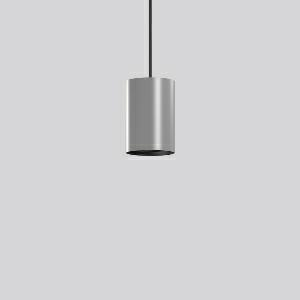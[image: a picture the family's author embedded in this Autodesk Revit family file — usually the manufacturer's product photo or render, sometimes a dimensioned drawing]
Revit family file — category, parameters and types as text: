
# Revit family: deecos_p_maxi_911538_004_3_76_b0c1
name_source: partatom
category: Lighting Fixtures
units: mm (PartAtom-declared; Revit-internal decimal feet)

## family parameters
Cut with Voids When Loaded = No
Host = Face
Light Source = No
Part Type = Normal
Room Calculation Point = No
Round Connector Dimension = Use Diameter
Shared = No

## types (1)
- DEECOS P maxi (1 x LED Modul 935, 4400 lm, 3500)
    Apparent Load = 35 VA
    Approval mark = CE
    CIE Flux Codes = 100 100 100 100 100
    Color Rendering = 92
    Color Temperature = 3500
    Default Elevation = 1800 mm
    Description = Series: DEECOS P maxi
Cylindrical pendant luminaire. Housing: die-cast aluminium, powder-coated. Canopy made of powder-coated sheet steel with magnetic attachment. Optical assembly with reflector made of MIRO-Silver with 98% total light reflection for outstanding efficiency - can be changed without tools. Best colour rendering index Ra>90. Transparent suspension cable 2 m, can be shortened. High quality converter without flickering and stroboscopic effect. The following accessories can be mounted without use of tools: interchangeable lenses, honeycomb louvre, clear and frosted diffusers, white interchangeable plastic ring. Decorative recessed suspension set available as accessory. 
Colour: silver
Diameter: 123 mm
Height: 181 mm
Suspension length: 2000 mm
Lamp: LED
Socket: without socket
Colour temperature: 3500K
Colour rendering index (CRI): 92
System power: 35 W
Rated luminous flux: 4400 lm
Luminous efficiency: 126 lm/W
Control gear: Converter, dimmable, DALI
Protection class: I
Type of protection: IP 20
    Height = 181 mm
    Lamp = 1 x LED Modul 935
    Lamp Light Flux = 4400 lm
    Lamp count = 1
    Length = 123 mm
    Lifetime = 50000 h
    Luminous efficacy = 126 lm/W
    Manufacturer = RZB
    ModVariant = No
    Model = 911538.004.3.76
    Mounting Place = Ceiling
    Mounting Type = Pendant
    Number of Poles = 1
    OnlyDefault = Yes
    Power Factor = 1
    Product Name = DEECOS P maxi
    Product group = Pendant luminaires
    ProductGroupID = 902
    Protection Class = Protection class I
    Protection Degree = IP 20
    RLX_Detail_Level = 1
    RLX_Emergency_Light_Flux = 0 lm
    RLX_Emergency_Type = 0
    RLX_Emergency_Type_DB = No
    RlxData = <blob elided: 35929 chars, md5=57ad862f>
    Socket = socket
    Standby Power = 0 W
    System Light Flux = 4400 lm
    System Power = 35 W
    Type Comments = Product without accessories
    Type Image = 911480.004.jpg
    URL = http://relux.com
    VarID = ---
    Voltage = 230 V
    Voltage Range = 220-240 V
    Weight = 0.00 kg
    Width = 0 mm  [stored 0 ft]

note: [stored X ft] marks values corroborated as IEEE doubles in the binary element streams (Revit-internal decimal feet)

## geometry (parser evidence)
native form markers: Blend x4, Sweep x10
no freeform markers — native parametric forms only
